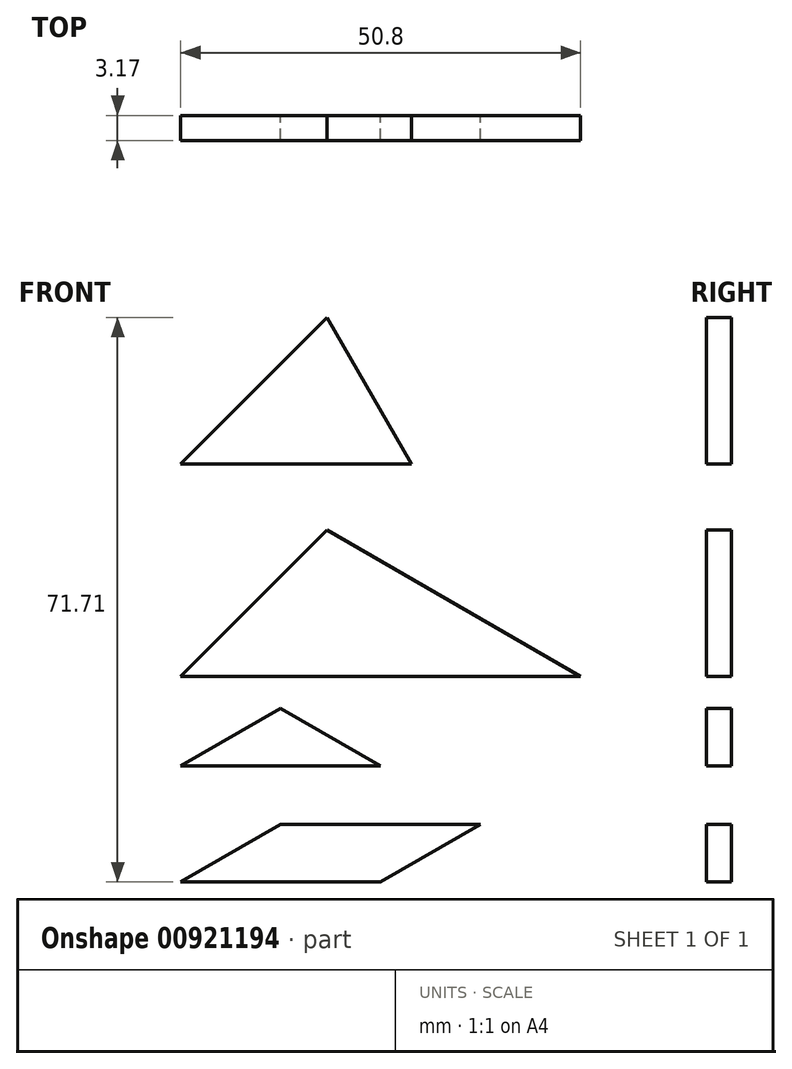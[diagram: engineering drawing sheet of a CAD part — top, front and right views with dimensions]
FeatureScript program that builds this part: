
annotation { "Feature Type Name" : "Feature", "Feature Type Description" : "" }
export const myFeature = defineFeature(function(context is Context, id is Id, definition is map)
    precondition{}
    {
        {
            var Q0;
            Q0=qCreatedBy(makeId("Front.planeOp"),FACE);
            var sketch = newSketch(context, id + "F0", { "sketchPlane" : qUnion([Q0])});
            skLineSegment(sketch, "E0", {"start": v(-69.88, -20.17) * mm, "end": v(-19.08, -20.17) * mm});
            skLineSegment(sketch, "E1", {"start": v(-69.88, -20.17) * mm, "end": v(-51.29, -1.58) * mm});
            skLineSegment(sketch, "E2", {"start": v(-51.29, -1.58) * mm, "end": v(-19.08, -20.17) * mm});
            skLineSegment(sketch, "E3", {"start": v(-69.88, -31.58) * mm, "end": v(-44.48, -31.58) * mm});
            skLineSegment(sketch, "E4", {"start": v(-44.48, -31.58) * mm, "end": v(-57.18, -24.25) * mm});
            skLineSegment(sketch, "E5", {"start": v(-57.18, -24.25) * mm, "end": v(-69.88, -31.58) * mm});
            skLineSegment(sketch, "E6", {"start": v(-69.88, -20.17) * mm, "end": v(-69.88, -54.72) * mm, "construction": true});
            skLineSegment(sketch, "E7", {"start": v(-69.88, -46.3) * mm, "end": v(-44.48, -46.3) * mm});
            skLineSegment(sketch, "E8", {"start": v(-69.88, -46.3) * mm, "end": v(-57.18, -38.96) * mm});
            skLineSegment(sketch, "E9", {"start": v(-57.18, -38.96) * mm, "end": v(-31.78, -38.96) * mm});
            skLineSegment(sketch, "E10", {"start": v(-31.78, -38.96) * mm, "end": v(-44.48, -46.3) * mm});
            skLineSegment(sketch, "E11", {"start": v(-69.88, 6.82) * mm, "end": v(-40.55, 6.82) * mm});
            skLineSegment(sketch, "E12", {"start": v(-40.55, 6.82) * mm, "end": v(-51.29, 25.41) * mm});
            skLineSegment(sketch, "E13", {"start": v(-51.29, 25.41) * mm, "end": v(-69.88, 6.82) * mm});
            skSolve(sketch);
        }
        {
            var Q0;
            Q0=makeQuery(id+"F0.imprint","IMPRINT",FACE,{"disambiguationData":[TD([[makeQuery(id+"F0.imprint","IMPRINT",EDGE,{"derivedFrom":sQuery(id+"F0.wireOp",EDGE,"E0")}),1.0]])]});
            extrude(context, id + "F1", {"entities" : qUnion([Q0]), "depth" : 3.17 * mm, "offsetDistance" : 25.4 * mm});
        }
        {
            var Q0;
            Q0=makeQuery(id+"F0.imprint","IMPRINT",FACE,{"disambiguationData":[TD([[makeQuery(id+"F0.imprint","IMPRINT",EDGE,{"derivedFrom":sQuery(id+"F0.wireOp",EDGE,"E3")}),1.0]])]});
            extrude(context, id + "F2", {"entities" : qUnion([Q0]), "depth" : 3.17 * mm, "offsetDistance" : 25.4 * mm});
        }
        {
            var Q0;
            Q0=makeQuery(id+"F0.imprint","IMPRINT",FACE,{"disambiguationData":[TD([[makeQuery(id+"F0.imprint","IMPRINT",EDGE,{"derivedFrom":sQuery(id+"F0.wireOp",EDGE,"E7")}),1.0]])]});
            extrude(context, id + "F3", {"entities" : qUnion([Q0]), "depth" : 3.17 * mm, "offsetDistance" : 25.4 * mm});
        }
        {
            var Q0;
            Q0=makeQuery(id+"F0.imprint","IMPRINT",FACE,{"disambiguationData":[TD([[makeQuery(id+"F0.imprint","IMPRINT",EDGE,{"derivedFrom":sQuery(id+"F0.wireOp",EDGE,"E11")}),1.0]])]});
            extrude(context, id + "F4", {"entities" : qUnion([Q0]), "depth" : 3.17 * mm, "offsetDistance" : 25.4 * mm});
        }
    });
